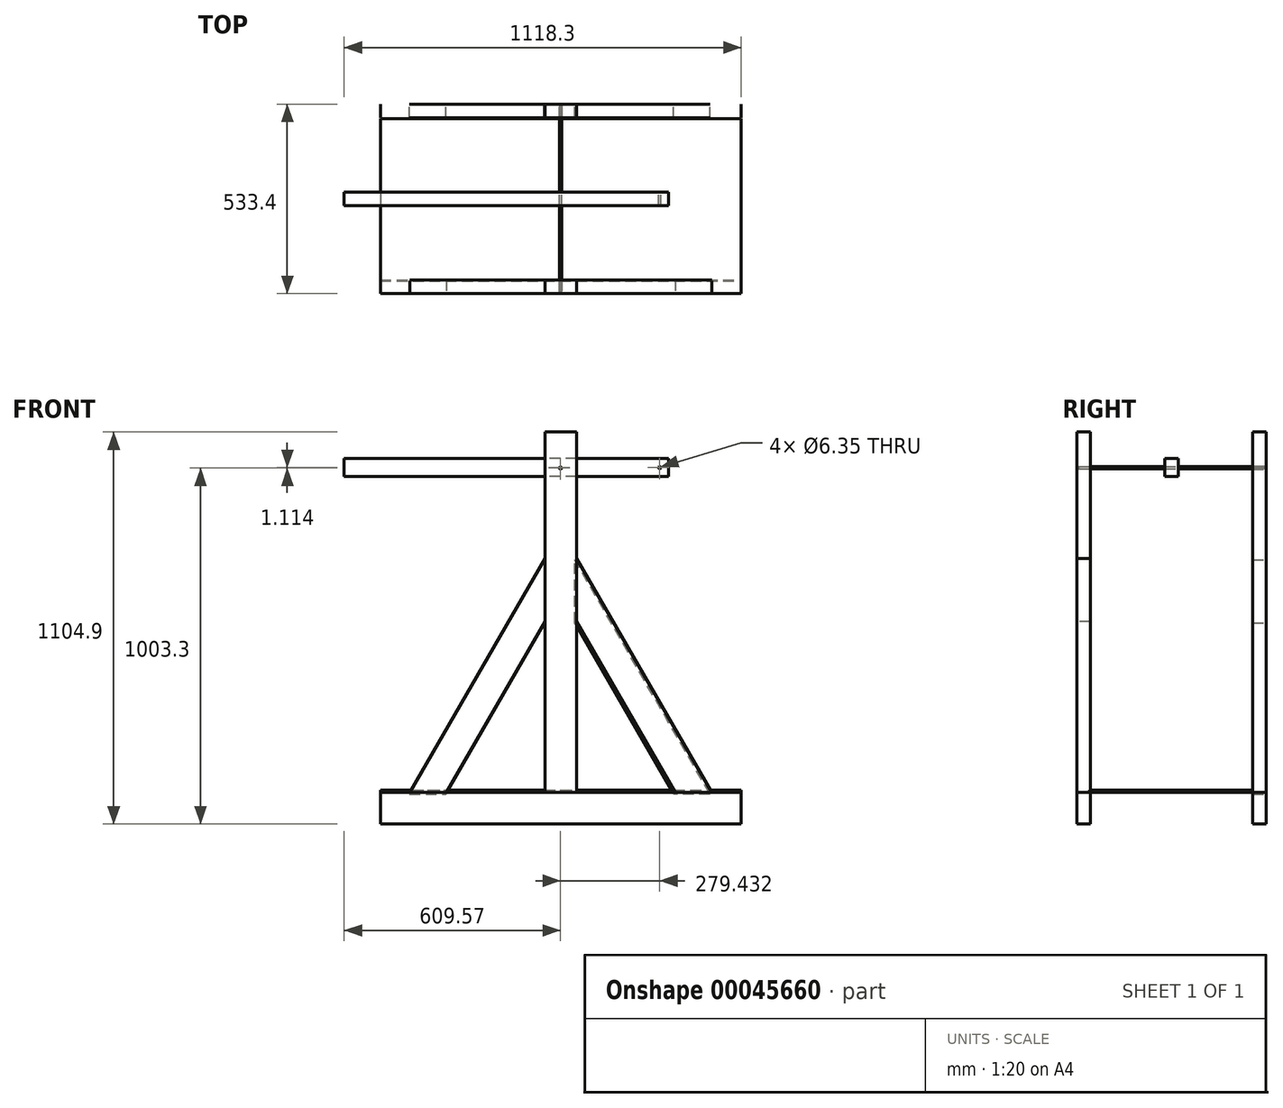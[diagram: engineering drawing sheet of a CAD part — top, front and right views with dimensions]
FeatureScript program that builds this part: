
annotation { "Feature Type Name" : "Feature", "Feature Type Description" : "" }
export const myFeature = defineFeature(function(context is Context, id is Id, definition is map)
    precondition{}
    {
        {
            var Q0;
            Q0=qCreatedBy(makeId("Top.planeOp"),FACE);
            var sketch = newSketch(context, id + "F0", { "sketchPlane" : qUnion([Q0])});
            skLineSegment(sketch, "E0.bottom", {"start": v(-507.38, 266.7) * mm, "end": v(508.62, 266.7) * mm});
            skLineSegment(sketch, "E0.top", {"start": v(-507.38, 228.6) * mm, "end": v(508.62, 228.6) * mm});
            skLineSegment(sketch, "E0.left", {"start": v(-507.38, 266.7) * mm, "end": v(-507.38, 228.6) * mm});
            skLineSegment(sketch, "E0.right", {"start": v(508.62, 266.7) * mm, "end": v(508.62, 228.6) * mm});
            skLineSegment(sketch, "E1.bottom", {"start": v(-507.38, -228.6) * mm, "end": v(508.62, -228.6) * mm});
            skLineSegment(sketch, "E1.top", {"start": v(-507.38, -266.7) * mm, "end": v(508.62, -266.7) * mm});
            skLineSegment(sketch, "E1.left", {"start": v(-507.38, -228.6) * mm, "end": v(-507.38, -266.7) * mm});
            skLineSegment(sketch, "E1.right", {"start": v(508.62, -228.6) * mm, "end": v(508.62, -266.7) * mm});
            skLineSegment(sketch, "E2.bottom", {"start": v(-507.38, 228.6) * mm, "end": v(-469.28, 228.6) * mm});
            skLineSegment(sketch, "E2.top", {"start": v(-507.38, -228.6) * mm, "end": v(-469.28, -228.6) * mm});
            skLineSegment(sketch, "E2.left", {"start": v(-507.38, 228.6) * mm, "end": v(-507.38, -228.6) * mm});
            skLineSegment(sketch, "E2.right", {"start": v(-469.28, 228.6) * mm, "end": v(-469.28, -228.6) * mm});
            skLineSegment(sketch, "E3.bottom", {"start": v(508.62, 228.6) * mm, "end": v(470.52, 228.6) * mm});
            skLineSegment(sketch, "E3.top", {"start": v(508.62, -228.6) * mm, "end": v(470.52, -228.6) * mm});
            skLineSegment(sketch, "E3.left", {"start": v(508.62, 228.6) * mm, "end": v(508.62, -228.6) * mm});
            skLineSegment(sketch, "E3.right", {"start": v(470.52, 228.6) * mm, "end": v(470.52, -228.6) * mm});
            skPoint(sketch, "E4", {"position": v(-469.28, 0) * mm});
            skPoint(sketch, "E5", {"position": v(470.52, 0) * mm});
            skSolve(sketch);
        }
        {
            var Q0;
            Q0=qCreatedBy(makeId("Top.planeOp"),FACE);
            var sketch = newSketch(context, id + "F1", { "sketchPlane" : qUnion([Q0])});
            skLineSegment(sketch, "E6.bottom", {"start": v(-507.38, 226.28) * mm, "end": v(508.73, 226.28) * mm});
            skLineSegment(sketch, "E6.top", {"start": v(-507.38, -230.92) * mm, "end": v(508.73, -230.92) * mm});
            skLineSegment(sketch, "E6.left", {"start": v(-507.38, 226.28) * mm, "end": v(-507.38, -230.92) * mm});
            skLineSegment(sketch, "E6.right", {"start": v(508.73, 226.28) * mm, "end": v(508.73, -230.92) * mm});
            skSolve(sketch);
        }
        {
            var Q0;
            Q0=makeQuery(id+"F0.imprint","IMPRINT",FACE,{"disambiguationData":[TD([[makeQuery(id+"F0.imprint","IMPRINT",EDGE,{"derivedFrom":sQuery(id+"F0.wireOp",EDGE,"E2.bottom")}),-1.0]])]});
            var Q1;
            Q1=makeQuery(id+"F0.imprint","IMPRINT",FACE,{"disambiguationData":[TD([[makeQuery(id+"F0.imprint","IMPRINT",EDGE,{"derivedFrom":sQuery(id+"F0.wireOp",EDGE,"E0.bottom")}),-1.0]])]});
            var Q2;
            Q2=makeQuery(id+"F0.imprint","IMPRINT",FACE,{"disambiguationData":[TD([[makeQuery(id+"F0.imprint","IMPRINT",EDGE,{"derivedFrom":sQuery(id+"F0.wireOp",EDGE,"E3.bottom")}),1.0]])]});
            var Q3;
            Q3=makeQuery(id+"F0.imprint","IMPRINT",FACE,{"disambiguationData":[TD([[makeQuery(id+"F0.imprint","IMPRINT",EDGE,{"derivedFrom":sQuery(id+"F0.wireOp",EDGE,"E1.bottom")}),-1.0]])]});
            extrude(context, id + "F2", {"entities" : qUnion([Q0, Q1, Q2, Q3]), "oppositeDirection" : true, "depth" : 88.9 * mm});
        }
        {
            var Q0;
            Q0=makeQuery(id+"F1.imprint","IMPRINT",FACE,{"disambiguationData":[TD([[makeQuery(id+"F1.imprint","IMPRINT",EDGE,{"derivedFrom":sQuery(id+"F1.wireOp",EDGE,"E6.bottom")}),-1.0]])]});
            extrude(context, id + "F3", {"entities" : qUnion([Q0]), "operationType" : NewBodyOperationType.ADD, "depth" : 6.35 * mm});
        }
        {
            var Q0;
            Q0=makeQuery(id+"F2.opExtrude","SWEPT_FACE",FACE,{"disambiguationData":[OSD([sQuery(id+"F0.wireOp",EDGE,"E0.bottom")])]});
            var sketch = newSketch(context, id + "F4", { "sketchPlane" : qUnion([Q0])});
            skLineSegment(sketch, "E7.top", {"start": v(-45.07, 1016) * mm, "end": v(43.83, 1016) * mm});
            skLineSegment(sketch, "E8", {"start": v(-45.07, 0) * mm, "end": v(43.83, 0) * mm});
            skLineSegment(sketch, "E9", {"start": v(-45.07, 1016) * mm, "end": v(-45.07, 0) * mm});
            skLineSegment(sketch, "E10", {"start": v(43.83, 0) * mm, "end": v(43.83, 1016) * mm});
            skPoint(sketch, "E11", {"position": v(0, 0) * mm});
            skPoint(sketch, "E12", {"position": v(-0.62, 0) * mm});
            skPoint(sketch, "E13", {"position": v(0, 914.4) * mm});
            skSolve(sketch);
        }
        {
            var Q0;
            Q0=makeQuery(id+"F2.opExtrude","SWEPT_FACE",FACE,{"disambiguationData":[OSD([sQuery(id+"F0.wireOp",EDGE,"E1.top")])]});
            var sketch = newSketch(context, id + "F5", { "sketchPlane" : qUnion([Q0])});
            skLineSegment(sketch, "E14.top", {"start": v(-43.83, 1016) * mm, "end": v(45.07, 1016) * mm});
            skLineSegment(sketch, "E15", {"start": v(-43.83, 0) * mm, "end": v(45.07, 0) * mm});
            skLineSegment(sketch, "E16", {"start": v(-43.83, 1016) * mm, "end": v(-43.83, 0) * mm});
            skLineSegment(sketch, "E17", {"start": v(45.07, 0) * mm, "end": v(45.07, 1016) * mm});
            skPoint(sketch, "E18", {"position": v(0.62, 0) * mm});
            skPoint(sketch, "E19", {"position": v(0, 914.4) * mm});
            skSolve(sketch);
        }
        {
            var Q0;
            Q0=makeQuery(id+"F5.imprint","IMPRINT",FACE,{"disambiguationData":[TD([[makeQuery(id+"F5.imprint","IMPRINT",EDGE,{"derivedFrom":sQuery(id+"F5.wireOp",EDGE,"E14.top")}),-1.0]])]});
            extrude(context, id + "F6", {"entities" : qUnion([Q0]), "oppositeDirection" : true, "depth" : 38.1 * mm});
        }
        {
            var Q0;
            Q0=makeQuery(id+"F4.imprint","IMPRINT",FACE,{"disambiguationData":[TD([[makeQuery(id+"F4.imprint","IMPRINT",EDGE,{"derivedFrom":sQuery(id+"F4.wireOp",EDGE,"E7.top")}),-1.0]])]});
            extrude(context, id + "F7", {"entities" : qUnion([Q0]), "oppositeDirection" : true, "depth" : 38.1 * mm});
        }
        {
            var Q0;
            {var subQ2=sQuery(id+"F5.wireOp",EDGE,"E15");Q0=makeQuery(id+"F5.imprint","IMPRINT",FACE,{"disambiguationData":[TD([[makeQuery(id+"F5.imprint","IMPRINT",EDGE,{"derivedFrom":subQ2}),-1.0]])]});}
            var sketch = newSketch(context, id + "F8", { "sketchPlane" : qUnion([Q0])});
            skLineSegment(sketch, "E20", {"start": v(-424.83, 0) * mm, "end": v(-43.83, 659.91) * mm});
            skLineSegment(sketch, "E21", {"start": v(-424.83, 0) * mm, "end": v(-322.18, 0) * mm});
            skLineSegment(sketch, "E22", {"start": v(-322.18, 0) * mm, "end": v(-43.83, 482.11) * mm});
            skLineSegment(sketch, "E23", {"start": v(-43.83, 482.11) * mm, "end": v(-43.83, 659.91) * mm});
            skLineSegment(sketch, "E24", {"start": v(45.07, 659.91) * mm, "end": v(426.07, 0) * mm});
            skLineSegment(sketch, "E25", {"start": v(426.07, 0) * mm, "end": v(323.42, 0) * mm});
            skLineSegment(sketch, "E26", {"start": v(323.42, 0) * mm, "end": v(45.07, 482.11) * mm});
            skLineSegment(sketch, "E27", {"start": v(45.07, 482.11) * mm, "end": v(45.07, 659.91) * mm});
            skSolve(sketch);
        }
        {
            var Q0;
            Q0=makeQuery(id+"F4.imprint","IMPRINT",FACE,{"disambiguationData":[TD([[makeQuery(id+"F4.imprint","IMPRINT",EDGE,{"derivedFrom":sQuery(id+"F4.wireOp",EDGE,"E7.top")}),-1.0]])]});
            var sketch = newSketch(context, id + "F9", { "sketchPlane" : qUnion([Q0])});
            skLineSegment(sketch, "E28", {"start": v(-421.2, -4.42) * mm, "end": v(-40.2, 655.49) * mm});
            skLineSegment(sketch, "E29", {"start": v(-421.2, -4.42) * mm, "end": v(-318.56, -4.42) * mm});
            skLineSegment(sketch, "E30", {"start": v(-318.56, -4.42) * mm, "end": v(-40.2, 477.69) * mm});
            skLineSegment(sketch, "E31", {"start": v(-40.2, 477.69) * mm, "end": v(-40.2, 655.49) * mm});
            skLineSegment(sketch, "E32", {"start": v(44.45, 655.49) * mm, "end": v(425.45, -4.42) * mm});
            skLineSegment(sketch, "E33", {"start": v(425.45, -4.42) * mm, "end": v(322.8, -4.42) * mm});
            skLineSegment(sketch, "E34", {"start": v(322.8, -4.42) * mm, "end": v(44.45, 477.69) * mm});
            skLineSegment(sketch, "E35", {"start": v(44.45, 477.69) * mm, "end": v(44.45, 655.49) * mm});
            skSolve(sketch);
        }
        {
            var Q0;
            Q0 = qSketchRegion(id + "F9", true);
            var Q1;
            {var subQ5=sQuery(id+"F9.wireOp",EDGE,"E29");Q1=makeQuery(id+"F9.imprint","IMPRINT",FACE,{"disambiguationData":[TD([[makeQuery(id+"F9.imprint","IMPRINT",EDGE,{"derivedFrom":subQ5}),1.0]])]});}
            var Q2;
            {var subQ5=sQuery(id+"F9.wireOp",EDGE,"E33");Q2=makeQuery(id+"F9.imprint","IMPRINT",FACE,{"disambiguationData":[TD([[makeQuery(id+"F9.imprint","IMPRINT",EDGE,{"derivedFrom":subQ5}),-1.0]])]});}
            extrude(context, id + "F10", {"entities" : qUnion([Q0, Q1, Q2]), "oppositeDirection" : true, "depth" : 38.1 * mm});
        }
        {
            var Q0;
            Q0=makeQuery(id+"F8.imprint","IMPRINT",FACE,{"disambiguationData":[TD([[makeQuery(id+"F8.imprint","IMPRINT",EDGE,{"derivedFrom":sQuery(id+"F8.wireOp",EDGE,"E20")}),-1.0]])]});
            var Q1;
            Q1=makeQuery(id+"F8.imprint","IMPRINT",FACE,{"disambiguationData":[TD([[makeQuery(id+"F8.imprint","IMPRINT",EDGE,{"derivedFrom":sQuery(id+"F8.wireOp",EDGE,"E24")}),-1.0]])]});
            extrude(context, id + "F11", {"entities" : qUnion([Q0, Q1]), "oppositeDirection" : true, "depth" : 38.1 * mm});
        }
        {
            var Q0;
            Q0=sQuery(id+"F5.wireOp",VERTEX,"E19");
            var Q1;
            Q1=makeQuery(id+"F6.opExtrude","SWEPT_BODY",BODY,{"disambiguationData":[OSD([sQuery(id+"F5.wireOp",EDGE,"E14.top"),sQuery(id+"F5.wireOp",EDGE,"E15"),sQuery(id+"F5.wireOp",EDGE,"E16"),sQuery(id+"F5.wireOp",EDGE,"E17")])]});
            hole(context, id + "F12", {"style" : HoleStyle.SIMPLE, "holeDiameter" : 6.35 * mm, "endStyle" : HoleEndStyle.THROUGH, "locations" : qUnion([Q0]), "scope" : qUnion([Q1])});
        }
        {
            var Q0;
            Q0=sQuery(id+"F4.wireOp",VERTEX,"E13");
            var Q1;
            Q1=makeQuery(id+"F7.opExtrude","SWEPT_BODY",BODY,{"disambiguationData":[OSD([sQuery(id+"F4.wireOp",EDGE,"E7.top"),sQuery(id+"F4.wireOp",EDGE,"E8"),sQuery(id+"F4.wireOp",EDGE,"E9"),sQuery(id+"F4.wireOp",EDGE,"E10")])]});
            hole(context, id + "F13", {"style" : HoleStyle.SIMPLE, "holeDiameter" : 6.35 * mm, "endStyle" : HoleEndStyle.THROUGH, "locations" : qUnion([Q0]), "scope" : qUnion([Q1])});
        }
        {
            var Q0;
            Q0=qCreatedBy(makeId("Front.planeOp"),FACE);
            var sketch = newSketch(context, id + "F14", { "sketchPlane" : qUnion([Q0])});
            skLineSegment(sketch, "E36.bottom", {"start": v(304.83, 890.11) * mm, "end": v(-609.57, 890.11) * mm});
            skLineSegment(sketch, "E36.top", {"start": v(304.83, 940.91) * mm, "end": v(-609.57, 940.91) * mm});
            skLineSegment(sketch, "E36.left", {"start": v(304.83, 940.91) * mm, "end": v(304.83, 890.11) * mm});
            skLineSegment(sketch, "E36.right", {"start": v(-609.57, 940.91) * mm, "end": v(-609.57, 890.11) * mm});
            skPoint(sketch, "E37", {"position": v(0.03, 915.51) * mm});
            skPoint(sketch, "E38", {"position": v(279.43, 915.51) * mm});
            skPoint(sketch, "E39", {"position": v(304.83, 915.51) * mm});
            skSolve(sketch);
        }
        {
            var Q0;
            Q0=makeQuery(id+"F14.imprint","IMPRINT",FACE,{"disambiguationData":[TD([[makeQuery(id+"F14.imprint","IMPRINT",EDGE,{"derivedFrom":sQuery(id+"F14.wireOp",EDGE,"E36.bottom")}),-1.0]])]});
            extrude(context, id + "F15", {"entities" : qUnion([Q0]), "endBound" : BoundingType.SYMMETRIC, "depth" : 38.1 * mm});
        }
        {
            var Q0;
            Q0=sQuery(id+"F14.wireOp",VERTEX,"E37");
            var Q1;
            Q1=makeQuery(id+"F15.opExtrude","SWEPT_BODY",BODY,{"disambiguationData":[OSD([sQuery(id+"F14.wireOp",EDGE,"E36.bottom"),sQuery(id+"F14.wireOp",EDGE,"E36.top"),sQuery(id+"F14.wireOp",EDGE,"E36.left"),sQuery(id+"F14.wireOp",EDGE,"E36.right")])]});
            hole(context, id + "F16", {"style" : HoleStyle.SIMPLE, "holeDiameter" : 6.35 * mm, "endStyle" : HoleEndStyle.THROUGH, "oppositeDirection" : true, "locations" : qUnion([Q0]), "scope" : qUnion([Q1])});
        }
        {
            var Q0;
            Q0=sQuery(id+"F14.wireOp",VERTEX,"E38");
            var Q1;
            Q1=makeQuery(id+"F15.opExtrude","SWEPT_BODY",BODY,{"disambiguationData":[OSD([sQuery(id+"F14.wireOp",EDGE,"E36.bottom"),sQuery(id+"F14.wireOp",EDGE,"E36.top"),sQuery(id+"F14.wireOp",EDGE,"E36.left"),sQuery(id+"F14.wireOp",EDGE,"E36.right")])]});
            hole(context, id + "F17", {"style" : HoleStyle.SIMPLE, "holeDiameter" : 6.35 * mm, "endStyle" : HoleEndStyle.THROUGH, "oppositeDirection" : true, "locations" : qUnion([Q0]), "scope" : qUnion([Q1])});
        }
        {
            var Q0;
            Q0=makeQuery(id+"F15.opExtrude","CAP_FACE",FACE,{"disambiguationData":[OSD([sQuery(id+"F14.wireOp",EDGE,"E36.bottom"),sQuery(id+"F14.wireOp",EDGE,"E36.top"),sQuery(id+"F14.wireOp",EDGE,"E36.left"),sQuery(id+"F14.wireOp",EDGE,"E36.right")])],"isStart":true});
            var sketch = newSketch(context, id + "F18", { "sketchPlane" : qUnion([Q0])});
            skCircle(sketch, "E40", {"center": v(0, 914.98) * mm, "radius": 3.18 * mm});
            skSolve(sketch);
        }
        {
            var Q0;
            Q0=sQuery(id+"F14.wireOp",VERTEX,"E37");
            var Q1;
            Q1=makeQuery(id+"F15.opExtrude","SWEPT_BODY",BODY,{"disambiguationData":[OSD([sQuery(id+"F14.wireOp",EDGE,"E36.bottom"),sQuery(id+"F14.wireOp",EDGE,"E36.top"),sQuery(id+"F14.wireOp",EDGE,"E36.left"),sQuery(id+"F14.wireOp",EDGE,"E36.right")])]});
            hole(context, id + "F19", {"style" : HoleStyle.SIMPLE, "holeDiameter" : 6.35 * mm, "endStyle" : HoleEndStyle.THROUGH, "locations" : qUnion([Q0]), "scope" : qUnion([Q1])});
        }
        {
            var Q0;
            Q0=sQuery(id+"F14.wireOp",VERTEX,"E38");
            var Q1;
            Q1=makeQuery(id+"F15.opExtrude","SWEPT_BODY",BODY,{"disambiguationData":[OSD([sQuery(id+"F14.wireOp",EDGE,"E36.bottom"),sQuery(id+"F14.wireOp",EDGE,"E36.top"),sQuery(id+"F14.wireOp",EDGE,"E36.left"),sQuery(id+"F14.wireOp",EDGE,"E36.right")])]});
            hole(context, id + "F20", {"style" : HoleStyle.SIMPLE, "holeDiameter" : 6.35 * mm, "endStyle" : HoleEndStyle.THROUGH, "locations" : qUnion([Q0]), "scope" : qUnion([Q1])});
        }
        {
            var Q0;
            Q0 = qSketchRegion(id + "F18", true);
            extrude(context, id + "F21", {"entities" : qUnion([Q0]), "depth" : 242.74 * mm});
        }
        {
            var Q0;
            Q0 = qSketchRegion(id + "F18", true);
            extrude(context, id + "F22", {"entities" : qUnion([Q0]), "oppositeDirection" : true, "depth" : 281.36 * mm});
        }
    });
